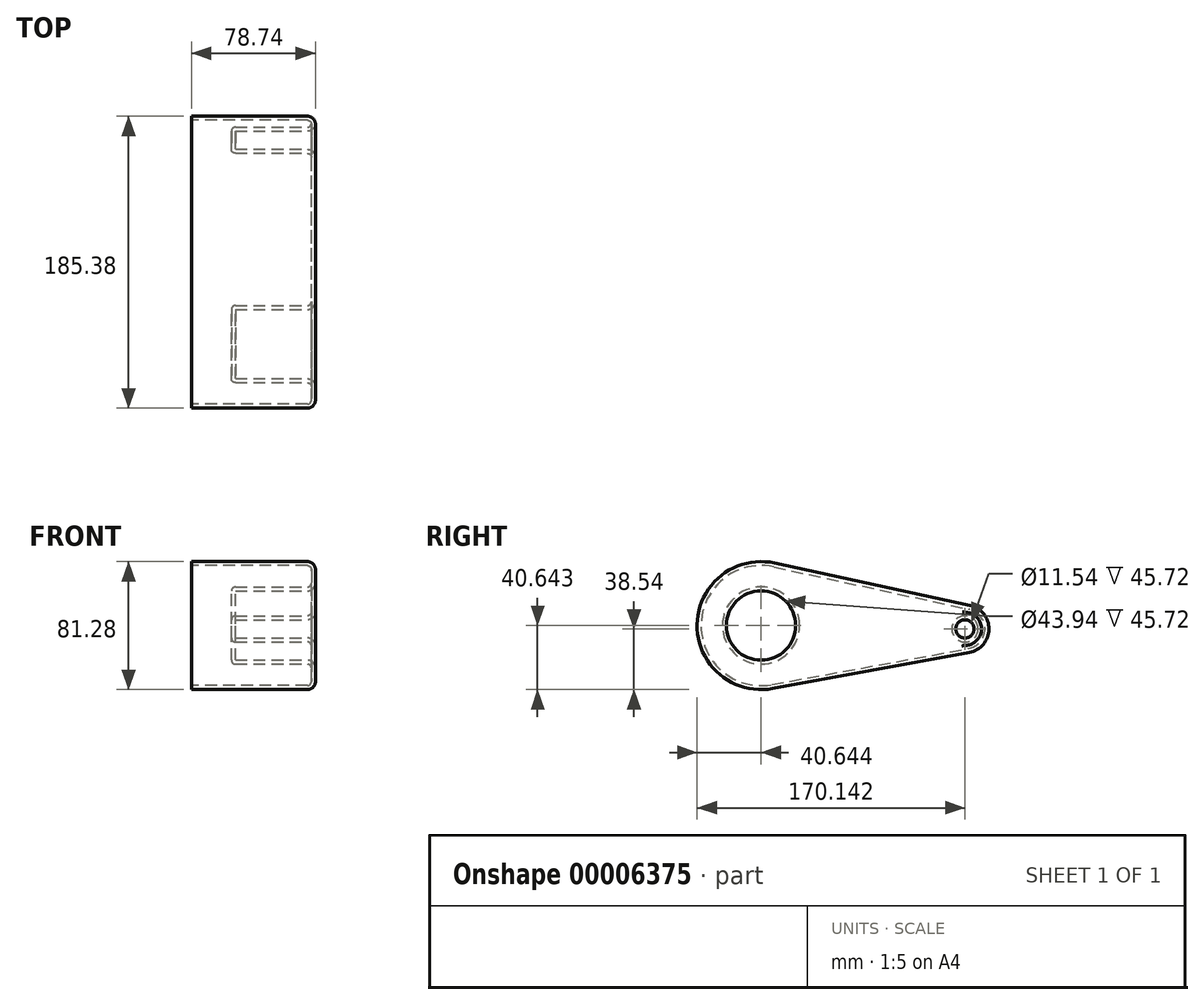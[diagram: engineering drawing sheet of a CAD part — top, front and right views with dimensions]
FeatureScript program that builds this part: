
annotation { "Feature Type Name" : "Feature", "Feature Type Description" : "" }
export const myFeature = defineFeature(function(context is Context, id is Id, definition is map)
    precondition{}
    {
        {
            var Q0;
            Q0=qCreatedBy(makeId("Right.planeOp"),FACE);
            var sketch = newSketch(context, id + "F0", { "sketchPlane" : qUnion([Q0])});
            skCircle(sketch, "E0", {"center": v(-79.13, 63.88) * mm, "radius": 38.1 * mm});
            skCircle(sketch, "E1", {"center": v(50.37, 61.78) * mm, "radius": 12.7 * mm});
            skLineSegment(sketch, "E2", {"start": v(-71.05, 101.12) * mm, "end": v(53.06, 74.2) * mm});
            skLineSegment(sketch, "E3", {"start": v(-72.26, 26.4) * mm, "end": v(52.66, 49.29) * mm});
            skSolve(sketch);
        }
        {
            var Q0;
            {var subQ0=sQuery(id+"F0.wireOp",EDGE,"E0");var subQ2=makeQuery(id+"F0.imprint","INTERSECT",VERTEX,{"derivedFrom":[subQ0,sQuery(id+"F0.wireOp",EDGE,"E2")]});Q0=makeQuery(id+"F0.imprint","IMPRINT",FACE,{"disambiguationData":[TD([[makeQuery(id+"F0.imprint","IMPRINT",EDGE,{"disambiguationData":[TD([[subQ2,-1.0]])],"derivedFrom":subQ0}),1.0]])]});}
            var Q1;
            {var subQ1=sQuery(id+"F0.wireOp",EDGE,"E2");Q1=makeQuery(id+"F0.imprint","IMPRINT",FACE,{"disambiguationData":[TD([[makeQuery(id+"F0.imprint","IMPRINT",EDGE,{"derivedFrom":subQ1}),-1.0]])]});}
            var Q2;
            {var subQ0=sQuery(id+"F0.wireOp",EDGE,"E1");var subQ2=makeQuery(id+"F0.imprint","INTERSECT",VERTEX,{"derivedFrom":[subQ0,sQuery(id+"F0.wireOp",EDGE,"E2")]});Q2=makeQuery(id+"F0.imprint","IMPRINT",FACE,{"disambiguationData":[TD([[makeQuery(id+"F0.imprint","IMPRINT",EDGE,{"disambiguationData":[TD([[subQ2,-1.0]])],"derivedFrom":subQ0}),1.0]])]});}
            extrude(context, id + "F1", {"entities" : qUnion([Q0, Q1, Q2]), "depth" : 76.2 * mm});
        }
        {
            var Q0;
            Q0=makeQuery(id+"F1.opExtrude","CAP_FACE",FACE,{"disambiguationData":[OSD([sQuery(id+"F0.wireOp",EDGE,"E0"),sQuery(id+"F0.wireOp",EDGE,"E1"),sQuery(id+"F0.wireOp",EDGE,"E2"),sQuery(id+"F0.wireOp",EDGE,"E3")])],"isStart":false});
            var sketch = newSketch(context, id + "F2", { "sketchPlane" : qUnion([Q0])});
            skCircle(sketch, "E4", {"center": v(-79.13, 63.88) * mm, "radius": 24.51 * mm});
            skCircle(sketch, "E5", {"center": v(50.37, 61.78) * mm, "radius": 8.31 * mm});
            skSolve(sketch);
        }
        {
            var Q0;
            Q0 = qSketchRegion(id + "F2", true);
            extrude(context, id + "F3", {"entities" : qUnion([Q0]), "operationType" : NewBodyOperationType.REMOVE, "oppositeDirection" : true, "depth" : 50.8 * mm});
        }
        {
            var Q0;
            Q0=makeQuery(id+"F3.boolean.opBoolean","COPY",EDGE,{"derivedFrom":makeQuery(id+"F3.opExtrude","CAP_EDGE",EDGE,{"disambiguationData":[OSD([sQuery(id+"F2.wireOp",EDGE,"E4")])],"isStart":true})});
            var Q1;
            Q1=makeQuery(id+"F3.boolean.opBoolean","COPY",EDGE,{"derivedFrom":makeQuery(id+"F3.opExtrude","CAP_EDGE",EDGE,{"disambiguationData":[OSD([sQuery(id+"F2.wireOp",EDGE,"E4")])],"isStart":false})});
            var Q2;
            Q2=makeQuery(id+"F1.opExtrude","CAP_EDGE",EDGE,{"disambiguationData":[OSD([sQuery(id+"F0.wireOp",EDGE,"E2")])],"isStart":false});
            var Q3;
            Q3=makeQuery(id+"F3.boolean.opBoolean","COPY",EDGE,{"derivedFrom":makeQuery(id+"F3.opExtrude","CAP_EDGE",EDGE,{"disambiguationData":[OSD([sQuery(id+"F2.wireOp",EDGE,"E5")])],"isStart":false})});
            var Q4;
            Q4=makeQuery(id+"F1.opExtrude","CAP_FACE",FACE,{"disambiguationData":[OSD([sQuery(id+"F0.wireOp",EDGE,"E0"),sQuery(id+"F0.wireOp",EDGE,"E1"),sQuery(id+"F0.wireOp",EDGE,"E2"),sQuery(id+"F0.wireOp",EDGE,"E3")])],"isStart":false});
            fillet(context, id + "F4", {"entities" : qUnion([Q0, Q1, Q2, Q3, Q4]), "radius" : 2.54 * mm, "tangentPropagation" : true, "allowEdgeOverflow" : false});
        }
        {
            var Q0;
            Q0=makeQuery(id+"F1.opExtrude","CAP_FACE",FACE,{"disambiguationData":[OSD([sQuery(id+"F0.wireOp",EDGE,"E0"),sQuery(id+"F0.wireOp",EDGE,"E1"),sQuery(id+"F0.wireOp",EDGE,"E2"),sQuery(id+"F0.wireOp",EDGE,"E3")])],"isStart":true});
            shell(context, id + "F5", {"entities" : qUnion([Q0]), "thickness" : 2.54 * mm, "oppositeDirection" : true});
        }
    });
